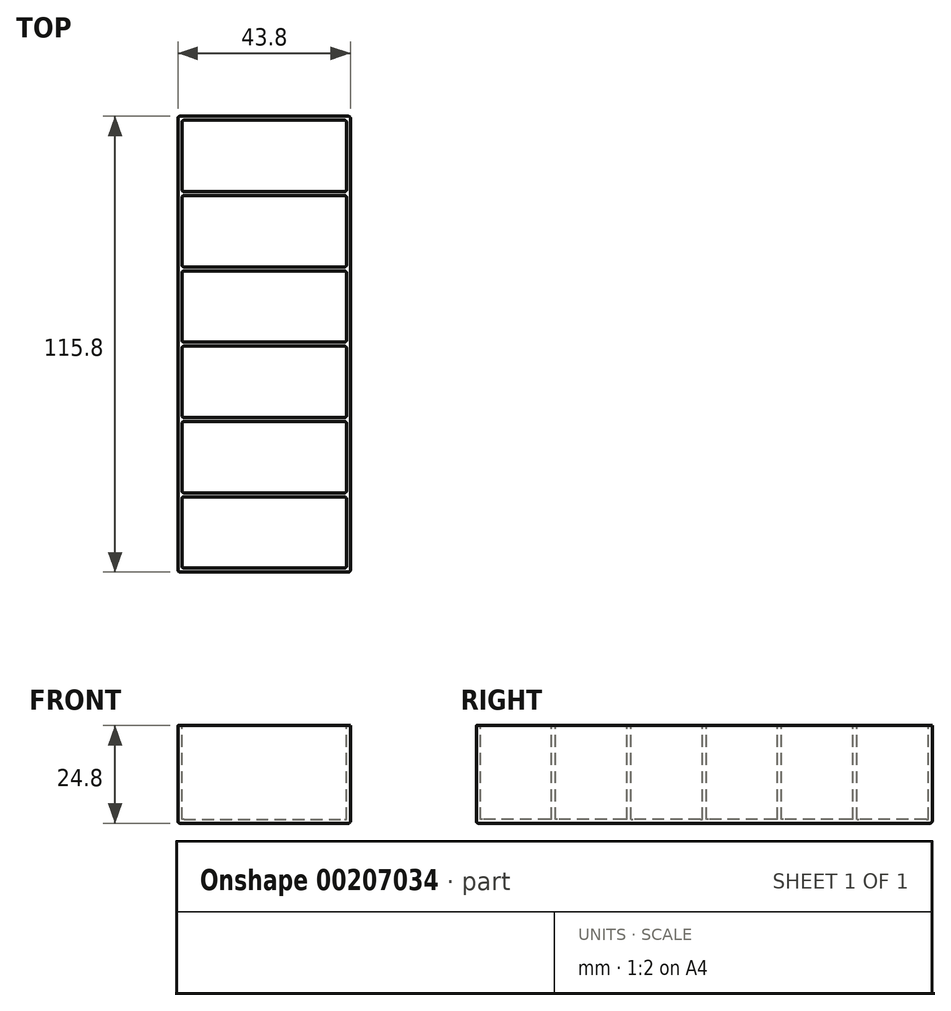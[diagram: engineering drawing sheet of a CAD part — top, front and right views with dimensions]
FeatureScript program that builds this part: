
annotation { "Feature Type Name" : "Feature", "Feature Type Description" : "" }
export const myFeature = defineFeature(function(context is Context, id is Id, definition is map)
    precondition{}
    {
        {
            var Q0;
            Q0=qCreatedBy(makeId("Top.planeOp"),FACE);
            var sketch = newSketch(context, id + "F0", { "sketchPlane" : qUnion([Q0])});
            skLineSegment(sketch, "E0.bottom", {"start": v(0, 0) * mm, "end": v(43.8, 0) * mm});
            skLineSegment(sketch, "E0.top", {"start": v(0, -115.8) * mm, "end": v(43.8, -115.8) * mm});
            skLineSegment(sketch, "E0.left", {"start": v(0, 0) * mm, "end": v(0, -115.8) * mm});
            skLineSegment(sketch, "E0.right", {"start": v(43.8, 0) * mm, "end": v(43.8, -115.8) * mm});
            skPoint(sketch, "E1.visualSharp", {"position": v(0, 0) * mm});
            skPoint(sketch, "E2.visualSharp", {"position": v(43.8, 0) * mm});
            skSolve(sketch);
        }
        {
            var Q0;
            Q0=makeQuery(id+"F0.imprint","IMPRINT",FACE,{"disambiguationData":[TD([[makeQuery(id+"F0.imprint","IMPRINT",EDGE,{"derivedFrom":sQuery(id+"F0.wireOp",EDGE,"E0.bottom")}),-1.0]])]});
            extrude(context, id + "F1", {"entities" : qUnion([Q0]), "depth" : 24.8 * mm});
        }
        {
            var Q0;
            Q0=makeQuery(id+"F1.opExtrude","CAP_FACE",FACE,{"disambiguationData":[OSD([sQuery(id+"F0.wireOp",EDGE,"E0.bottom"),sQuery(id+"F0.wireOp",EDGE,"E0.top"),sQuery(id+"F0.wireOp",EDGE,"E0.left"),sQuery(id+"F0.wireOp",EDGE,"E0.right")])],"isStart":false});
            var sketch = newSketch(context, id + "F2", { "sketchPlane" : qUnion([Q0])});
            skLineSegment(sketch, "E3.bottom", {"start": v(1, -1) * mm, "end": v(42.8, -1) * mm});
            skLineSegment(sketch, "E3.top", {"start": v(1, -19.13) * mm, "end": v(42.8, -19.13) * mm});
            skLineSegment(sketch, "E3.left", {"start": v(1, -1) * mm, "end": v(1, -19.13) * mm});
            skLineSegment(sketch, "E3.right", {"start": v(42.8, -1) * mm, "end": v(42.8, -19.13) * mm});
            skLineSegment(sketch, "E4.bottom", {"start": v(1, -20.13) * mm, "end": v(42.8, -20.13) * mm});
            skLineSegment(sketch, "E4.top", {"start": v(1, -38.27) * mm, "end": v(42.8, -38.27) * mm});
            skLineSegment(sketch, "E4.left", {"start": v(1, -20.13) * mm, "end": v(1, -38.27) * mm});
            skLineSegment(sketch, "E4.right", {"start": v(42.8, -20.13) * mm, "end": v(42.8, -38.27) * mm});
            skLineSegment(sketch, "E5.bottom", {"start": v(1, -39.27) * mm, "end": v(42.8, -39.27) * mm});
            skLineSegment(sketch, "E5.top", {"start": v(1, -57.4) * mm, "end": v(42.8, -57.4) * mm});
            skLineSegment(sketch, "E5.left", {"start": v(1, -39.27) * mm, "end": v(1, -57.4) * mm});
            skLineSegment(sketch, "E5.right", {"start": v(42.8, -39.27) * mm, "end": v(42.8, -57.4) * mm});
            skLineSegment(sketch, "E6.bottom", {"start": v(1, -58.4) * mm, "end": v(42.8, -58.4) * mm});
            skLineSegment(sketch, "E6.top", {"start": v(1, -76.53) * mm, "end": v(42.8, -76.53) * mm});
            skLineSegment(sketch, "E6.left", {"start": v(1, -58.4) * mm, "end": v(1, -76.53) * mm});
            skLineSegment(sketch, "E6.right", {"start": v(42.8, -58.4) * mm, "end": v(42.8, -76.53) * mm});
            skLineSegment(sketch, "E7.bottom", {"start": v(1, -77.53) * mm, "end": v(42.8, -77.53) * mm});
            skLineSegment(sketch, "E7.top", {"start": v(1, -95.67) * mm, "end": v(42.8, -95.67) * mm});
            skLineSegment(sketch, "E7.left", {"start": v(1, -77.53) * mm, "end": v(1, -95.67) * mm});
            skLineSegment(sketch, "E7.right", {"start": v(42.8, -77.53) * mm, "end": v(42.8, -95.67) * mm});
            skLineSegment(sketch, "E8.bottom", {"start": v(1, -96.67) * mm, "end": v(42.8, -96.67) * mm});
            skLineSegment(sketch, "E8.top", {"start": v(1, -114.8) * mm, "end": v(42.8, -114.8) * mm});
            skLineSegment(sketch, "E8.left", {"start": v(1, -96.67) * mm, "end": v(1, -114.8) * mm});
            skLineSegment(sketch, "E8.right", {"start": v(42.8, -96.67) * mm, "end": v(42.8, -114.8) * mm});
            skSolve(sketch);
        }
        {
            var Q0;
            Q0=makeQuery(id+"F2.imprint","IMPRINT",FACE,{"disambiguationData":[TD([[makeQuery(id+"F2.imprint","IMPRINT",EDGE,{"derivedFrom":sQuery(id+"F2.wireOp",EDGE,"E3.bottom")}),-1.0]])]});
            var Q1;
            Q1=makeQuery(id+"F2.imprint","IMPRINT",FACE,{"disambiguationData":[TD([[makeQuery(id+"F2.imprint","IMPRINT",EDGE,{"derivedFrom":sQuery(id+"F2.wireOp",EDGE,"E4.bottom")}),-1.0]])]});
            var Q2;
            Q2=makeQuery(id+"F2.imprint","IMPRINT",FACE,{"disambiguationData":[TD([[makeQuery(id+"F2.imprint","IMPRINT",EDGE,{"derivedFrom":sQuery(id+"F2.wireOp",EDGE,"E5.bottom")}),-1.0]])]});
            var Q3;
            Q3=makeQuery(id+"F2.imprint","IMPRINT",FACE,{"disambiguationData":[TD([[makeQuery(id+"F2.imprint","IMPRINT",EDGE,{"derivedFrom":sQuery(id+"F2.wireOp",EDGE,"E6.bottom")}),-1.0]])]});
            var Q4;
            Q4=makeQuery(id+"F2.imprint","IMPRINT",FACE,{"disambiguationData":[TD([[makeQuery(id+"F2.imprint","IMPRINT",EDGE,{"derivedFrom":sQuery(id+"F2.wireOp",EDGE,"E7.bottom")}),-1.0]])]});
            var Q5;
            Q5=makeQuery(id+"F2.imprint","IMPRINT",FACE,{"disambiguationData":[TD([[makeQuery(id+"F2.imprint","IMPRINT",EDGE,{"derivedFrom":sQuery(id+"F2.wireOp",EDGE,"E8.bottom")}),-1.0]])]});
            extrude(context, id + "F3", {"entities" : qUnion([Q0, Q1, Q2, Q3, Q4, Q5]), "operationType" : NewBodyOperationType.REMOVE, "oppositeDirection" : true, "depth" : 23.8 * mm});
        }
        {
            var Q0;
            Q0=makeQuery(id+"F1.opExtrude","SWEPT_EDGE",EDGE,{"disambiguationData":[OSD([sQuery(id+"F0.wireOp",EDGE,"E0.bottom"),sQuery(id+"F0.wireOp",EDGE,"E0.right")])]});
            var Q1;
            Q1=makeQuery(id+"F1.opExtrude","SWEPT_EDGE",EDGE,{"disambiguationData":[OSD([sQuery(id+"F0.wireOp",EDGE,"E0.top"),sQuery(id+"F0.wireOp",EDGE,"E0.right")])]});
            var Q2;
            Q2=makeQuery(id+"F1.opExtrude","SWEPT_EDGE",EDGE,{"disambiguationData":[OSD([sQuery(id+"F0.wireOp",EDGE,"E0.top"),sQuery(id+"F0.wireOp",EDGE,"E0.left")])]});
            var Q3;
            Q3=makeQuery(id+"F1.opExtrude","SWEPT_EDGE",EDGE,{"disambiguationData":[OSD([sQuery(id+"F0.wireOp",EDGE,"E0.bottom"),sQuery(id+"F0.wireOp",EDGE,"E0.left")])]});
            var Q4;
            Q4=makeQuery(id+"F1.opExtrude","CAP_EDGE",EDGE,{"disambiguationData":[OSD([sQuery(id+"F0.wireOp",EDGE,"E0.left")])],"isStart":true});
            var Q5;
            Q5=makeQuery(id+"F1.opExtrude","CAP_EDGE",EDGE,{"disambiguationData":[OSD([sQuery(id+"F0.wireOp",EDGE,"E0.top")])],"isStart":true});
            var Q6;
            Q6=makeQuery(id+"F1.opExtrude","CAP_EDGE",EDGE,{"disambiguationData":[OSD([sQuery(id+"F0.wireOp",EDGE,"E0.bottom")])],"isStart":true});
            var Q7;
            Q7=makeQuery(id+"F1.opExtrude","CAP_EDGE",EDGE,{"disambiguationData":[OSD([sQuery(id+"F0.wireOp",EDGE,"E0.right")])],"isStart":true});
            fillet(context, id + "F4", {"entities" : qUnion([Q0, Q1, Q2, Q3, Q4, Q5, Q6, Q7]), "radius" : .5 * mm, "tangentPropagation" : true, "allowEdgeOverflow" : false});
        }
        {
            var Q0;
            Q0=makeQuery(id+"F3.boolean.opBoolean","COPY",EDGE,{"derivedFrom":makeQuery(id+"F3.opExtrude","SWEPT_EDGE",EDGE,{"disambiguationData":[OSD([sQuery(id+"F2.wireOp",EDGE,"E3.bottom"),sQuery(id+"F2.wireOp",EDGE,"E3.left")])]})});
            var Q1;
            Q1=makeQuery(id+"F3.boolean.opBoolean","COPY",EDGE,{"derivedFrom":makeQuery(id+"F3.opExtrude","SWEPT_EDGE",EDGE,{"disambiguationData":[OSD([sQuery(id+"F2.wireOp",EDGE,"E3.bottom"),sQuery(id+"F2.wireOp",EDGE,"E3.right")])]})});
            var Q2;
            Q2=makeQuery(id+"F3.boolean.opBoolean","COPY",EDGE,{"derivedFrom":makeQuery(id+"F3.opExtrude","SWEPT_EDGE",EDGE,{"disambiguationData":[OSD([sQuery(id+"F2.wireOp",EDGE,"E4.bottom"),sQuery(id+"F2.wireOp",EDGE,"E4.right")])]})});
            var Q3;
            Q3=makeQuery(id+"F3.boolean.opBoolean","COPY",EDGE,{"derivedFrom":makeQuery(id+"F3.opExtrude","SWEPT_EDGE",EDGE,{"disambiguationData":[OSD([sQuery(id+"F2.wireOp",EDGE,"E5.bottom"),sQuery(id+"F2.wireOp",EDGE,"E5.right")])]})});
            var Q4;
            Q4=makeQuery(id+"F3.boolean.opBoolean","COPY",EDGE,{"derivedFrom":makeQuery(id+"F3.opExtrude","SWEPT_EDGE",EDGE,{"disambiguationData":[OSD([sQuery(id+"F2.wireOp",EDGE,"E6.bottom"),sQuery(id+"F2.wireOp",EDGE,"E6.right")])]})});
            var Q5;
            Q5=makeQuery(id+"F3.boolean.opBoolean","COPY",EDGE,{"derivedFrom":makeQuery(id+"F3.opExtrude","SWEPT_EDGE",EDGE,{"disambiguationData":[OSD([sQuery(id+"F2.wireOp",EDGE,"E7.bottom"),sQuery(id+"F2.wireOp",EDGE,"E7.right")])]})});
            var Q6;
            Q6=makeQuery(id+"F3.boolean.opBoolean","COPY",EDGE,{"derivedFrom":makeQuery(id+"F3.opExtrude","SWEPT_EDGE",EDGE,{"disambiguationData":[OSD([sQuery(id+"F2.wireOp",EDGE,"E8.bottom"),sQuery(id+"F2.wireOp",EDGE,"E8.right")])]})});
            var Q7;
            Q7=makeQuery(id+"F3.boolean.opBoolean","COPY",EDGE,{"derivedFrom":makeQuery(id+"F3.opExtrude","SWEPT_EDGE",EDGE,{"disambiguationData":[OSD([sQuery(id+"F2.wireOp",EDGE,"E8.top"),sQuery(id+"F2.wireOp",EDGE,"E8.right")])]})});
            var Q8;
            Q8=makeQuery(id+"F3.boolean.opBoolean","COPY",EDGE,{"derivedFrom":makeQuery(id+"F3.opExtrude","SWEPT_EDGE",EDGE,{"disambiguationData":[OSD([sQuery(id+"F2.wireOp",EDGE,"E8.top"),sQuery(id+"F2.wireOp",EDGE,"E8.left")])]})});
            var Q9;
            Q9=makeQuery(id+"F3.boolean.opBoolean","COPY",EDGE,{"derivedFrom":makeQuery(id+"F3.opExtrude","SWEPT_EDGE",EDGE,{"disambiguationData":[OSD([sQuery(id+"F2.wireOp",EDGE,"E7.top"),sQuery(id+"F2.wireOp",EDGE,"E7.left")])]})});
            var Q10;
            Q10=makeQuery(id+"F3.boolean.opBoolean","COPY",EDGE,{"derivedFrom":makeQuery(id+"F3.opExtrude","SWEPT_EDGE",EDGE,{"disambiguationData":[OSD([sQuery(id+"F2.wireOp",EDGE,"E6.top"),sQuery(id+"F2.wireOp",EDGE,"E6.left")])]})});
            var Q11;
            Q11=makeQuery(id+"F3.boolean.opBoolean","COPY",EDGE,{"derivedFrom":makeQuery(id+"F3.opExtrude","SWEPT_EDGE",EDGE,{"disambiguationData":[OSD([sQuery(id+"F2.wireOp",EDGE,"E5.top"),sQuery(id+"F2.wireOp",EDGE,"E5.left")])]})});
            var Q12;
            Q12=makeQuery(id+"F3.boolean.opBoolean","COPY",EDGE,{"derivedFrom":makeQuery(id+"F3.opExtrude","SWEPT_EDGE",EDGE,{"disambiguationData":[OSD([sQuery(id+"F2.wireOp",EDGE,"E4.top"),sQuery(id+"F2.wireOp",EDGE,"E4.left")])]})});
            var Q13;
            Q13=makeQuery(id+"F3.boolean.opBoolean","COPY",EDGE,{"derivedFrom":makeQuery(id+"F3.opExtrude","SWEPT_EDGE",EDGE,{"disambiguationData":[OSD([sQuery(id+"F2.wireOp",EDGE,"E3.top"),sQuery(id+"F2.wireOp",EDGE,"E3.left")])]})});
            fillet(context, id + "F5", {"entities" : qUnion([Q0, Q1, Q2, Q3, Q4, Q5, Q6, Q7, Q8, Q9, Q10, Q11, Q12, Q13]), "radius" : .5 * mm, "tangentPropagation" : true, "allowEdgeOverflow" : false});
        }
        {
            var Q0;
            Q0=makeQuery(id+"F3.boolean.opBoolean","COPY",EDGE,{"derivedFrom":makeQuery(id+"F3.opExtrude","SWEPT_EDGE",EDGE,{"disambiguationData":[OSD([sQuery(id+"F2.wireOp",EDGE,"E3.top"),sQuery(id+"F2.wireOp",EDGE,"E3.right")])]})});
            var Q1;
            Q1=makeQuery(id+"F3.boolean.opBoolean","COPY",EDGE,{"derivedFrom":makeQuery(id+"F3.opExtrude","SWEPT_EDGE",EDGE,{"disambiguationData":[OSD([sQuery(id+"F2.wireOp",EDGE,"E4.top"),sQuery(id+"F2.wireOp",EDGE,"E4.right")])]})});
            var Q2;
            Q2=makeQuery(id+"F3.boolean.opBoolean","COPY",EDGE,{"derivedFrom":makeQuery(id+"F3.opExtrude","SWEPT_EDGE",EDGE,{"disambiguationData":[OSD([sQuery(id+"F2.wireOp",EDGE,"E5.top"),sQuery(id+"F2.wireOp",EDGE,"E5.right")])]})});
            var Q3;
            Q3=makeQuery(id+"F3.boolean.opBoolean","COPY",EDGE,{"derivedFrom":makeQuery(id+"F3.opExtrude","SWEPT_EDGE",EDGE,{"disambiguationData":[OSD([sQuery(id+"F2.wireOp",EDGE,"E4.bottom"),sQuery(id+"F2.wireOp",EDGE,"E4.left")])]})});
            var Q4;
            Q4=makeQuery(id+"F3.boolean.opBoolean","COPY",EDGE,{"derivedFrom":makeQuery(id+"F3.opExtrude","SWEPT_EDGE",EDGE,{"disambiguationData":[OSD([sQuery(id+"F2.wireOp",EDGE,"E5.bottom"),sQuery(id+"F2.wireOp",EDGE,"E5.left")])]})});
            var Q5;
            Q5=makeQuery(id+"F3.boolean.opBoolean","COPY",EDGE,{"derivedFrom":makeQuery(id+"F3.opExtrude","SWEPT_EDGE",EDGE,{"disambiguationData":[OSD([sQuery(id+"F2.wireOp",EDGE,"E6.bottom"),sQuery(id+"F2.wireOp",EDGE,"E6.left")])]})});
            var Q6;
            Q6=makeQuery(id+"F3.boolean.opBoolean","COPY",EDGE,{"derivedFrom":makeQuery(id+"F3.opExtrude","SWEPT_EDGE",EDGE,{"disambiguationData":[OSD([sQuery(id+"F2.wireOp",EDGE,"E6.top"),sQuery(id+"F2.wireOp",EDGE,"E6.right")])]})});
            var Q7;
            Q7=makeQuery(id+"F3.boolean.opBoolean","COPY",EDGE,{"derivedFrom":makeQuery(id+"F3.opExtrude","SWEPT_EDGE",EDGE,{"disambiguationData":[OSD([sQuery(id+"F2.wireOp",EDGE,"E7.top"),sQuery(id+"F2.wireOp",EDGE,"E7.right")])]})});
            var Q8;
            Q8=makeQuery(id+"F3.boolean.opBoolean","COPY",EDGE,{"derivedFrom":makeQuery(id+"F3.opExtrude","SWEPT_EDGE",EDGE,{"disambiguationData":[OSD([sQuery(id+"F2.wireOp",EDGE,"E7.bottom"),sQuery(id+"F2.wireOp",EDGE,"E7.left")])]})});
            var Q9;
            Q9=makeQuery(id+"F3.boolean.opBoolean","COPY",EDGE,{"derivedFrom":makeQuery(id+"F3.opExtrude","SWEPT_EDGE",EDGE,{"disambiguationData":[OSD([sQuery(id+"F2.wireOp",EDGE,"E8.bottom"),sQuery(id+"F2.wireOp",EDGE,"E8.left")])]})});
            fillet(context, id + "F6", {"entities" : qUnion([Q0, Q1, Q2, Q3, Q4, Q5, Q6, Q7, Q8, Q9]), "radius" : .5 * mm, "tangentPropagation" : true, "allowEdgeOverflow" : false});
        }
    });
